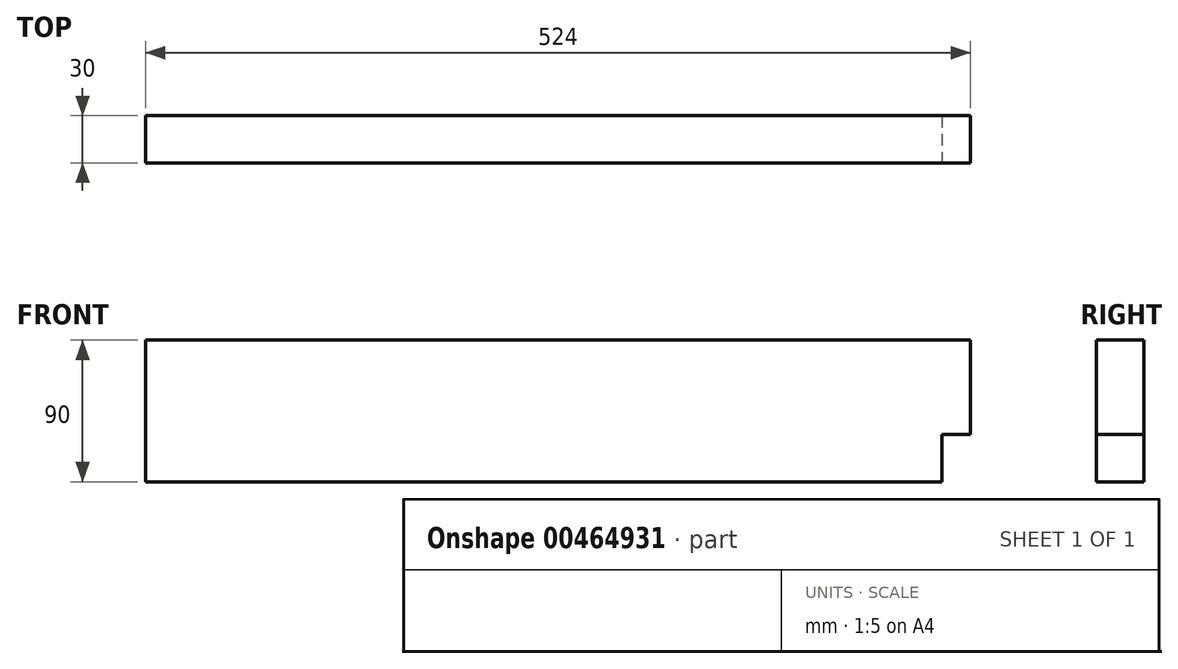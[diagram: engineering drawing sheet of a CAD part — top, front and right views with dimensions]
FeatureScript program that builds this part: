
annotation { "Feature Type Name" : "Feature", "Feature Type Description" : "" }
export const myFeature = defineFeature(function(context is Context, id is Id, definition is map)
    precondition{}
    {
        {
            var Q0;
            Q0=qCreatedBy(makeId("Right.planeOp"),FACE);
            var sketch = newSketch(context, id + "F0", { "sketchPlane" : qUnion([Q0])});
            skLineSegment(sketch, "E0.bottom", {"start": v(-15, 45) * mm, "end": v(15, 45) * mm});
            skLineSegment(sketch, "E0.top", {"start": v(-15, -45) * mm, "end": v(15, -45) * mm});
            skLineSegment(sketch, "E0.left", {"start": v(-15, 45) * mm, "end": v(-15, -45) * mm});
            skLineSegment(sketch, "E0.right", {"start": v(15, 45) * mm, "end": v(15, -45) * mm});
            skPoint(sketch, "E0.middle", {"position": v(0, 0) * mm});
            skSolve(sketch);
        }
        {
            var Q0;
            Q0=makeQuery(id+"F0.imprint","IMPRINT",FACE,{"disambiguationData":[TD([[makeQuery(id+"F0.imprint","IMPRINT",EDGE,{"derivedFrom":sQuery(id+"F0.wireOp",EDGE,"E0.bottom")}),-1.0]])]});
            extrude(context, id + "F1", {"entities" : qUnion([Q0]), "endBound" : BoundingType.SYMMETRIC, "depth" : 524 * mm, "offsetDistance" : 25 * mm});
        }
        {
            var Q0;
            Q0=makeQuery(id+"F1.opExtrude","SWEPT_FACE",FACE,{"disambiguationData":[OSD([sQuery(id+"F0.wireOp",EDGE,"E0.left")])]});
            var sketch = newSketch(context, id + "F2", { "sketchPlane" : qUnion([Q0])});
            skLineSegment(sketch, "E1.bottom", {"start": v(262, -45) * mm, "end": v(244, -45) * mm});
            skLineSegment(sketch, "E1.top", {"start": v(262, -15) * mm, "end": v(244, -15) * mm});
            skLineSegment(sketch, "E1.left", {"start": v(262, -45) * mm, "end": v(262, -15) * mm});
            skLineSegment(sketch, "E1.right", {"start": v(244, -45) * mm, "end": v(244, -15) * mm});
            skSolve(sketch);
        }
        {
            var Q0;
            Q0=makeQuery(id+"F2.imprint","IMPRINT",FACE,{"disambiguationData":[TD([[makeQuery(id+"F2.imprint","IMPRINT",EDGE,{"derivedFrom":sQuery(id+"F2.wireOp",EDGE,"E1.bottom")}),-1.0]])]});
            extrude(context, id + "F3", {"entities" : qUnion([Q0]), "operationType" : NewBodyOperationType.REMOVE, "oppositeDirection" : true, "depth" : 30 * mm, "offsetDistance" : 25 * mm});
        }
    });
